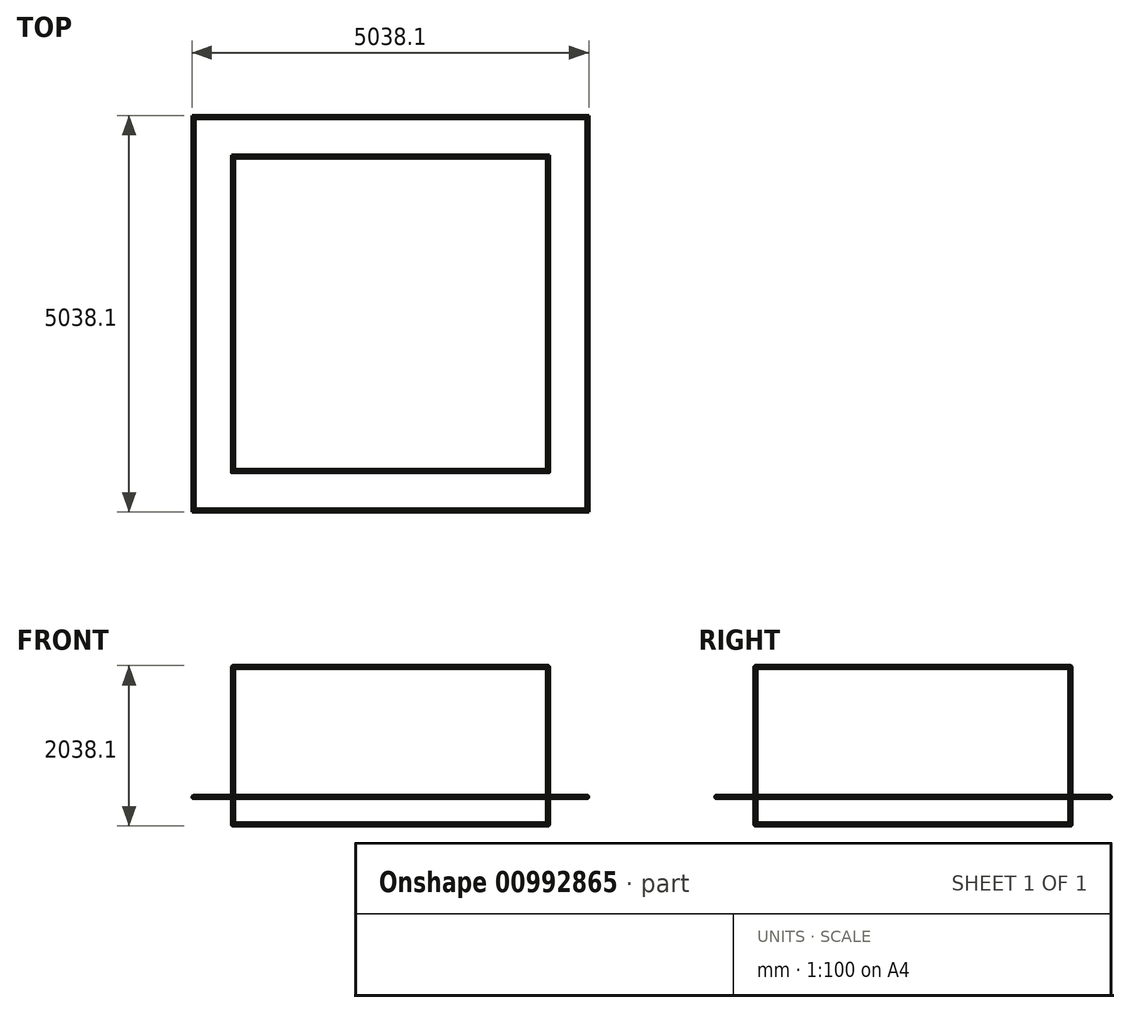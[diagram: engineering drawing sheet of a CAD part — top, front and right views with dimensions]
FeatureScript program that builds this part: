
annotation { "Feature Type Name" : "Feature", "Feature Type Description" : "" }
export const myFeature = defineFeature(function(context is Context, id is Id, definition is map)
    precondition{}
    {
        {
            var Q0;
            Q0=qCreatedBy(makeId("Top.planeOp"),FACE);
            var sketch = newSketch(context, id + "F0", { "sketchPlane" : qUnion([Q0])});
            skLineSegment(sketch, "E0.bottom", {"start": v(-2000, 2000) * mm, "end": v(2000, 2000) * mm});
            skLineSegment(sketch, "E0.top", {"start": v(-2000, -2000) * mm, "end": v(2000, -2000) * mm});
            skLineSegment(sketch, "E0.left", {"start": v(-2000, 2000) * mm, "end": v(-2000, -2000) * mm});
            skLineSegment(sketch, "E0.right", {"start": v(2000, 2000) * mm, "end": v(2000, -2000) * mm});
            skPoint(sketch, "E0.middle", {"position": v(0, 0) * mm});
            skSolve(sketch);
        }
        {
            var Q0;
            Q0=qCreatedBy(makeId("Front.planeOp"),FACE);
            var sketch = newSketch(context, id + "F1", { "sketchPlane" : qUnion([Q0])});
            skCircle(sketch, "E1", {"center": v(2000, 0) * mm, "radius": 19.05 * mm});
            skSolve(sketch);
        }
        {
            var Q0;
            Q0 = qSketchRegion(id + "F1", true);
            var Q1;
            Q1=sQuery(id+"F0.wireOp",EDGE,"E0.right");
            var Q2;
            Q2=sQuery(id+"F0.wireOp",EDGE,"E0.top");
            var Q3;
            Q3=sQuery(id+"F0.wireOp",EDGE,"E0.left");
            var Q4;
            Q4=sQuery(id+"F0.wireOp",EDGE,"E0.bottom");
            sweep(context, id + "F2", {"profiles" : qUnion([Q0]), "path" : qUnion([Q1, Q2, Q3, Q4])});
        }
        {
            var Q0;
            Q0=makeQuery(id+"F2.opSweep","SWEPT_BODY",BODY,{"disambiguationData":[OSD([sQuery(id+"F0.wireOp",EDGE,"E0.bottom"),sQuery(id+"F1.wireOp",EDGE,"E1")])]});
            transform(context, id + "F3", {"entities" : qUnion([Q0]), "transformType" : TransformType.TRANSLATION_3D, "dx" : 0 * mm, "dy" : 0 * mm, "dz" : 2000 * mm, "makeCopy" : true});
        }
        {
            var Q0;
            Q0=makeQuery(id+"F0.imprint","IMPRINT",FACE,{"disambiguationData":[TD([[makeQuery(id+"F0.imprint","IMPRINT",EDGE,{"derivedFrom":sQuery(id+"F0.wireOp",EDGE,"E0.bottom")}),-1.0]])]});
            var sketch = newSketch(context, id + "F4", { "sketchPlane" : qUnion([Q0])});
            skCircle(sketch, "E2", {"center": v(-1999.34, -2000.86) * mm, "radius": 19.05 * mm});
            skSolve(sketch);
        }
        {
            var Q0;
            Q0 = qSketchRegion(id + "F4", true);
            extrude(context, id + "F5", {"entities" : qUnion([Q0]), "depth" : 2000 * mm, "offsetDistance" : 25 * mm});
        }
        {
            var Q0;
            Q0=makeQuery(id+"F5.opExtrude","SWEPT_BODY",BODY,{"disambiguationData":[OSD([sQuery(id+"F4.wireOp",EDGE,"E2")])]});
            transform(context, id + "F6", {"entities" : qUnion([Q0]), "transformType" : TransformType.TRANSLATION_3D, "dx" : 4000 * mm, "dy" : 4000 * mm, "dz" : 0 * mm, "makeCopy" : true});
        }
        {
            var Q0;
            Q0=makeQuery(id+"F5.opExtrude","SWEPT_BODY",BODY,{"disambiguationData":[OSD([sQuery(id+"F4.wireOp",EDGE,"E2")])]});
            transform(context, id + "F7", {"entities" : qUnion([Q0]), "transformType" : TransformType.TRANSLATION_3D, "dx" : 4000 * mm, "dy" : 0 * mm, "dz" : 0 * mm, "makeCopy" : false});
        }
        {
            var Q0;
            Q0=makeQuery(id+"F5.opExtrude","SWEPT_BODY",BODY,{"disambiguationData":[OSD([sQuery(id+"F4.wireOp",EDGE,"E2")])]});
            var Q1;
            Q1=makeQuery(id+"F6.opPattern","COPY",BODY,{"derivedFrom":makeQuery(id+"F5.opExtrude","SWEPT_BODY",BODY,{"disambiguationData":[OSD([sQuery(id+"F4.wireOp",EDGE,"E2")])]}),"instanceName":"1"});
            transform(context, id + "F8", {"entities" : qUnion([Q0, Q1]), "transformType" : TransformType.TRANSLATION_3D, "dx" : -4000 * mm, "dy" : 0 * mm, "dz" : 0 * mm, "makeCopy" : true});
        }
        {
            var Q0;
            Q0=qCreatedBy(makeId("Top.planeOp"),FACE);
            var sketch = newSketch(context, id + "F9", { "sketchPlane" : qUnion([Q0])});
            skLineSegment(sketch, "E3.bottom", {"start": v(2500, 2500) * mm, "end": v(-2500, 2500) * mm});
            skLineSegment(sketch, "E3.top", {"start": v(2500, -2500) * mm, "end": v(-2500, -2500) * mm});
            skLineSegment(sketch, "E3.left", {"start": v(2500, 2500) * mm, "end": v(2500, -2500) * mm});
            skLineSegment(sketch, "E3.right", {"start": v(-2500, 2500) * mm, "end": v(-2500, -2500) * mm});
            skPoint(sketch, "E3.middle", {"position": v(0, 0) * mm});
            skSolve(sketch);
        }
        {
            var Q0;
            Q0=qCreatedBy(makeId("Front.planeOp"),FACE);
            var sketch = newSketch(context, id + "F10", { "sketchPlane" : qUnion([Q0])});
            skCircle(sketch, "E4", {"center": v(2500, 0) * mm, "radius": 19.05 * mm});
            skSolve(sketch);
        }
        {
            var Q0;
            Q0=makeQuery(id+"F10.imprint","IMPRINT",FACE,{"disambiguationData":[TD([[makeQuery(id+"F10.imprint","IMPRINT",EDGE,{"derivedFrom":sQuery(id+"F10.wireOp",EDGE,"E4")}),1.0]])]});
            var Q1;
            Q1=sQuery(id+"F9.wireOp",EDGE,"E3.left");
            var Q2;
            Q2=sQuery(id+"F9.wireOp",EDGE,"E3.top");
            var Q3;
            Q3=sQuery(id+"F9.wireOp",EDGE,"E3.bottom");
            var Q4;
            Q4=sQuery(id+"F9.wireOp",EDGE,"E3.right");
            sweep(context, id + "F11", {"profiles" : qUnion([Q0]), "path" : qUnion([Q1, Q2, Q3, Q4])});
        }
        {
            var Q0;
            Q0=makeQuery(id+"F2.opSweep","SWEPT_BODY",BODY,{"disambiguationData":[OSD([sQuery(id+"F0.wireOp",EDGE,"E0.bottom"),sQuery(id+"F1.wireOp",EDGE,"E1")])]});
            transform(context, id + "F12", {"entities" : qUnion([Q0]), "transformType" : TransformType.TRANSLATION_3D, "dx" : 0 * mm, "dy" : 0 * mm, "dz" : 350 * mm, "makeCopy" : true});
        }
        {
            var Q0;
            Q0=makeQuery(id+"F11.opSweep","SWEPT_BODY",BODY,{"disambiguationData":[OSD([sQuery(id+"F9.wireOp",EDGE,"E3.bottom"),sQuery(id+"F10.wireOp",EDGE,"E4")])]});
            transform(context, id + "F13", {"entities" : qUnion([Q0]), "transformType" : TransformType.TRANSLATION_3D, "dx" : 0 * mm, "dy" : 0 * mm, "dz" : 350 * mm, "makeCopy" : false});
        }
    });
